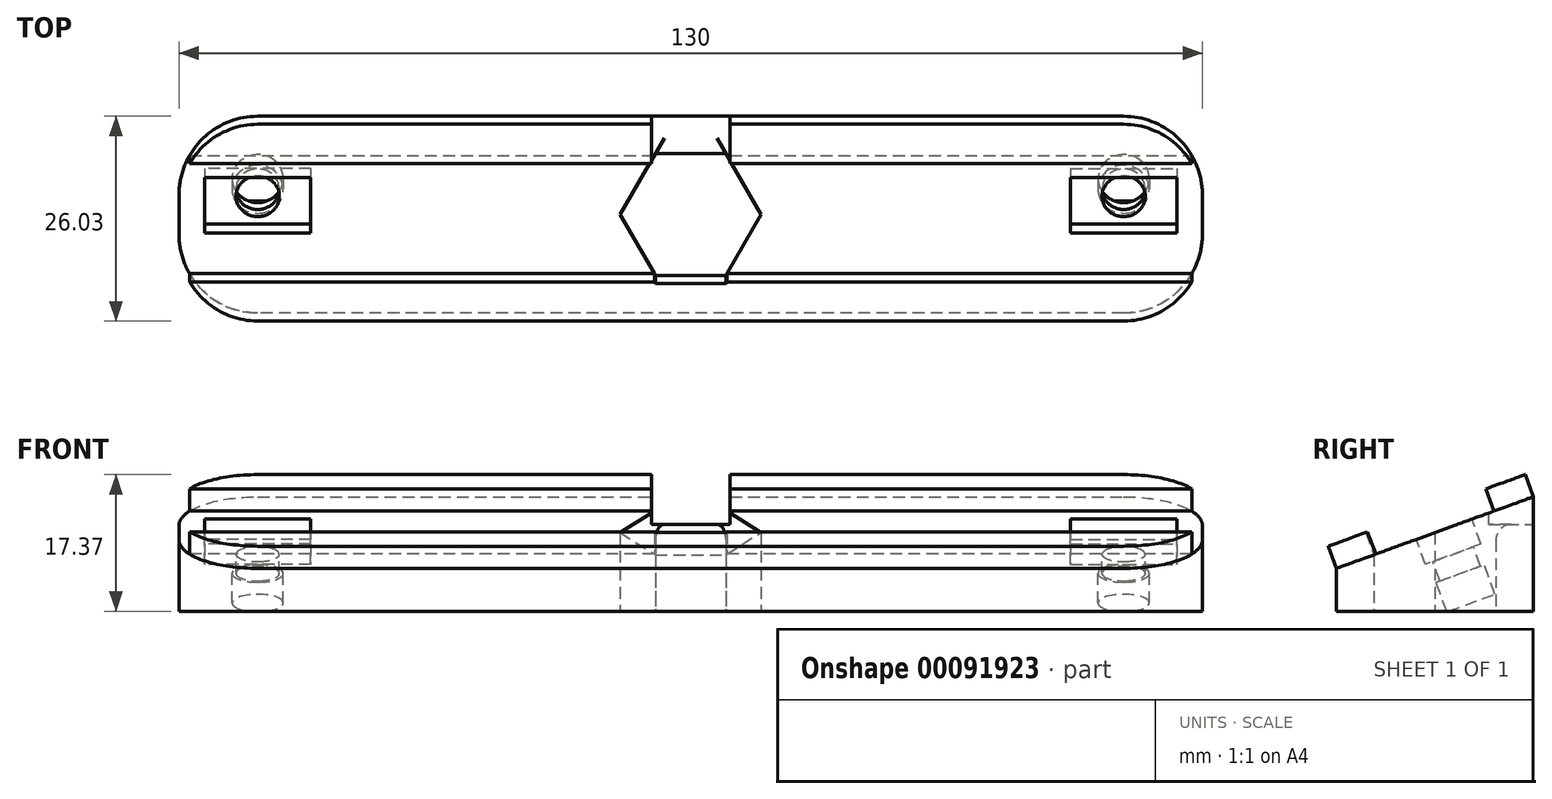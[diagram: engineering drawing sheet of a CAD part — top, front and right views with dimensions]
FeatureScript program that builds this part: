
annotation { "Feature Type Name" : "Feature", "Feature Type Description" : "" }
export const myFeature = defineFeature(function(context is Context, id is Id, definition is map)
    precondition{}
    {
        {
            var Q0;
            Q0=qCreatedBy(makeId("Front.planeOp"),FACE);
            var sketch = newSketch(context, id + "F0", { "sketchPlane" : qUnion([Q0])});
            skLineSegment(sketch, "E0", {"start": v(-41.25, 10) * mm, "end": v(39.47, 10) * mm, "construction": true});
            skSolve(sketch);
        }
        {
            var Q0;
            Q0=sQuery(id+"F0.wireOp",EDGE,"E0");
            cPlane(context, id + "F1", {"entities" : qUnion([Q0]), "cplaneType" : CPlaneType.LINE_ANGLE, "offset" : 150 * mm, "angle" : 290 * degree, "width" : 150 * mm, "height" : 150 * mm});
        }
        {
            var Q0;
            Q0=qCreatedBy(makeId("Top.planeOp"),FACE);
            var sketch = newSketch(context, id + "F2", { "sketchPlane" : qUnion([Q0])});
            skLineSegment(sketch, "E1.bottom", {"start": v(55, 12.5) * mm, "end": v(-55, 12.5) * mm});
            skLineSegment(sketch, "E1.top", {"start": v(55, -12.5) * mm, "end": v(-55, -12.5) * mm});
            skLineSegment(sketch, "E1.left", {"start": v(65, 2.5) * mm, "end": v(65, -2.5) * mm});
            skLineSegment(sketch, "E1.right", {"start": v(-65, 2.5) * mm, "end": v(-65, -2.5) * mm});
            skPoint(sketch, "E1.middle", {"position": v(0, 0) * mm});
            skPoint(sketch, "E2.visualSharp", {"position": v(-65, 12.5) * mm});
            skArc(sketch, "E2.filletArc", {"start": v(-55, 12.5) * mm, "mid": v(-62.07, 9.57) * mm, "end": v(-65, 2.5) * mm});
            skPoint(sketch, "E3.visualSharp", {"position": v(-65, -12.5) * mm});
            skArc(sketch, "E3.filletArc", {"start": v(-65, -2.5) * mm, "mid": v(-62.07, -9.57) * mm, "end": v(-55, -12.5) * mm});
            skPoint(sketch, "E4.visualSharp", {"position": v(65, 12.5) * mm});
            skArc(sketch, "E4.filletArc", {"start": v(65, 2.5) * mm, "mid": v(62.07, 9.57) * mm, "end": v(55, 12.5) * mm});
            skPoint(sketch, "E5.visualSharp", {"position": v(65, -12.5) * mm});
            skArc(sketch, "E5.filletArc", {"start": v(55, -12.5) * mm, "mid": v(62.07, -9.57) * mm, "end": v(65, -2.5) * mm});
            skSolve(sketch);
        }
        {
            var Q0;
            Q0 = qSketchRegion(id + "F2", true);
            var Q1;
            Q1=qCreatedBy(id+"F1.planeOp",FACE);
            extrude(context, id + "F3", {"entities" : qUnion([Q0]), "endBound" : BoundingType.UP_TO_SURFACE, "endBoundEntityFace" : qUnion([Q1]), "depth" : 5.6 * mm});
        }
        {
            var Q0;
            Q0=makeQuery(id+"F3.opExtrude","CAP_FACE",FACE,{"disambiguationData":[OSD([sQuery(id+"F2.wireOp",EDGE,"E1.bottom"),sQuery(id+"F2.wireOp",EDGE,"E1.top"),sQuery(id+"F2.wireOp",EDGE,"E1.left"),sQuery(id+"F2.wireOp",EDGE,"E1.right"),sQuery(id+"F2.wireOp",EDGE,"E2.filletArc"),sQuery(id+"F2.wireOp",EDGE,"E3.filletArc"),sQuery(id+"F2.wireOp",EDGE,"E4.filletArc"),sQuery(id+"F2.wireOp",EDGE,"E5.filletArc")])],"isStart":true});
            var sketch = newSketch(context, id + "F4", { "sketchPlane" : qUnion([Q0])});
            skCircle(sketch, "E6.cCircle", {"center": v(0, 0) * mm, "radius": 7.75 * mm, "construction": true});
            skLineSegment(sketch, "E6.0", {"start": v(4.47, 7.75) * mm, "end": v(8.95, 0) * mm});
            skLineSegment(sketch, "E6.1", {"start": v(8.95, 0) * mm, "end": v(4.47, -7.75) * mm});
            skLineSegment(sketch, "E6.2", {"start": v(4.47, -7.75) * mm, "end": v(-4.47, -7.75) * mm});
            skLineSegment(sketch, "E6.3", {"start": v(-4.47, -7.75) * mm, "end": v(-8.95, 0) * mm});
            skLineSegment(sketch, "E6.4", {"start": v(-8.95, 0) * mm, "end": v(-4.47, 7.75) * mm});
            skLineSegment(sketch, "E6.5", {"start": v(-4.47, 7.75) * mm, "end": v(4.47, 7.75) * mm});
            skPoint(sketch, "E6.0.midPoint", {"position": v(6.71, 3.88) * mm});
            skSolve(sketch);
        }
        {
            var Q0;
            Q0 = qSketchRegion(id + "F4", true);
            extrude(context, id + "F5", {"entities" : qUnion([Q0]), "operationType" : NewBodyOperationType.REMOVE, "endBound" : BoundingType.THROUGH_ALL, "oppositeDirection" : true, "depth" : 7 * mm});
        }
        {
            var Q0;
            Q0=makeQuery(id+"F3.opExtrude","CAP_FACE",FACE,{"disambiguationData":[OSD([sQuery(id+"F2.wireOp",EDGE,"E1.bottom"),sQuery(id+"F2.wireOp",EDGE,"E1.top"),sQuery(id+"F2.wireOp",EDGE,"E1.left"),sQuery(id+"F2.wireOp",EDGE,"E1.right"),sQuery(id+"F2.wireOp",EDGE,"E2.filletArc"),sQuery(id+"F2.wireOp",EDGE,"E3.filletArc"),sQuery(id+"F2.wireOp",EDGE,"E4.filletArc"),sQuery(id+"F2.wireOp",EDGE,"E5.filletArc")])],"isStart":false});
            var sketch = newSketch(context, id + "F6", { "sketchPlane" : qUnion([Q0])});
            skLineSegment(sketch, "E7", {"start": v(-65, 11.42) * mm, "end": v(65, 11.42) * mm});
            skLineSegment(sketch, "E8", {"start": v(65, -4.58) * mm, "end": v(-65, -4.58) * mm});
            skPoint(sketch, "E9", {"position": v(-65, 3.42) * mm});
            skPoint(sketch, "E10", {"position": v(65, 3.42) * mm});
            skLineSegment(sketch, "E11", {"start": v(-65, 3.42) * mm, "end": v(65, 3.42) * mm, "construction": true});
            skSolve(sketch);
        }
        {
            var Q0;
            {var subQ0=sQuery(id+"F6.wireOp",EDGE,"E7");Q0=makeQuery(id+"F6.imprint","IMPRINT",FACE,{"disambiguationData":[TD([[makeQuery(id+"F6.imprint","IMPRINT",EDGE,{"derivedFrom":subQ0}),1.0]])]});}
            var Q1;
            {var subQ0=sQuery(id+"F6.wireOp",EDGE,"E8");Q1=makeQuery(id+"F6.imprint","IMPRINT",FACE,{"disambiguationData":[TD([[makeQuery(id+"F6.imprint","IMPRINT",EDGE,{"derivedFrom":subQ0}),1.0]])]});}
            extrude(context, id + "F7", {"entities" : qUnion([Q0, Q1]), "operationType" : NewBodyOperationType.ADD, "depth" : 3 * mm});
        }
        {
            var Q0;
            {var subQ1=sQuery(id+"F2.wireOp",EDGE,"E5.filletArc");var subQ2=sQuery(id+"F2.wireOp",EDGE,"E4.filletArc");var subQ3=sQuery(id+"F2.wireOp",EDGE,"E3.filletArc");var subQ4=sQuery(id+"F2.wireOp",EDGE,"E2.filletArc");var subQ5=sQuery(id+"F2.wireOp",EDGE,"E1.right");var subQ6=sQuery(id+"F2.wireOp",EDGE,"E1.left");var subQ7=sQuery(id+"F2.wireOp",EDGE,"E1.top");var subQ8=sQuery(id+"F2.wireOp",EDGE,"E1.bottom");var subQ12=makeQuery(id+"F3.opExtrude","CAP_FACE",FACE,{"disambiguationData":[OSD([subQ8,subQ7,subQ6,subQ5,subQ4,subQ3,subQ2,subQ1])],"isStart":false});var subQ15=subQ12;Q0=qUnion([makeQuery(id+"F7.boolean.opBoolean","SPLIT",FACE,{"disambiguationData":[TD([makeQuery(id+"F3.opExtrude","SWEPT_FACE",FACE,{"disambiguationData":[OSD([subQ6])]})])],"derivedFrom":subQ15}),makeQuery(id+"F7.boolean.opBoolean","SPLIT",FACE,{"disambiguationData":[TD([makeQuery(id+"F3.opExtrude","SWEPT_FACE",FACE,{"disambiguationData":[OSD([subQ5])]})])],"derivedFrom":subQ15})]);}
            var sketch = newSketch(context, id + "F8", { "sketchPlane" : qUnion([Q0])});
            skLineSegment(sketch, "E12.bottom", {"start": v(-48.25, 8.42) * mm, "end": v(-61.75, 8.42) * mm});
            skLineSegment(sketch, "E12.top", {"start": v(-48.25, 0.92) * mm, "end": v(-61.75, 0.92) * mm});
            skLineSegment(sketch, "E12.left", {"start": v(-48.25, 8.42) * mm, "end": v(-48.25, 0.92) * mm});
            skLineSegment(sketch, "E12.right", {"start": v(-61.75, 8.42) * mm, "end": v(-61.75, 0.92) * mm});
            skPoint(sketch, "E12.middle", {"position": v(-55, 4.67) * mm});
            skLineSegment(sketch, "E13.MirrorCS", {"start": v(48.25, 0.92) * mm, "end": v(61.75, 0.92) * mm});
            skLineSegment(sketch, "E14.MirrorCS", {"start": v(48.25, 8.42) * mm, "end": v(61.75, 8.42) * mm});
            skLineSegment(sketch, "E15.MirrorCS", {"start": v(61.75, 8.42) * mm, "end": v(61.75, 0.92) * mm});
            skLineSegment(sketch, "E16.MirrorCS", {"start": v(48.25, 8.42) * mm, "end": v(48.25, 0.92) * mm});
            skPoint(sketch, "E17.MirrorP", {"position": v(55, 4.67) * mm});
            skSolve(sketch);
        }
        {
            var Q0;
            Q0 = qSketchRegion(id + "F8", true);
            extrude(context, id + "F9", {"entities" : qUnion([Q0]), "operationType" : NewBodyOperationType.REMOVE, "oppositeDirection" : true, "depth" : 3.38 * mm});
        }
        {
            var Q0;
            Q0=makeQuery(id+"F9.boolean.opBoolean","COPY",FACE,{"derivedFrom":makeQuery(id+"F9.opExtrude","CAP_FACE",FACE,{"disambiguationData":[OSD([sQuery(id+"F8.wireOp",EDGE,"E12.bottom"),sQuery(id+"F8.wireOp",EDGE,"E12.top"),sQuery(id+"F8.wireOp",EDGE,"E12.left"),sQuery(id+"F8.wireOp",EDGE,"E12.right")])],"isStart":false})});
            var sketch = newSketch(context, id + "F10", { "sketchPlane" : qUnion([Q0])});
            skCircle(sketch, "E18", {"center": v(-55, 4.67) * mm, "radius": 2.75 * mm});
            skPoint(sketch, "E18.centerSnap0", {"position": v(-48.25, 4.67) * mm});
            skPoint(sketch, "E18.centerSnap1", {"position": v(-55, 8.42) * mm});
            skCircle(sketch, "E19.MirrorC", {"center": v(55, 4.67) * mm, "radius": 2.75 * mm});
            skSolve(sketch);
        }
        {
            var Q0;
            Q0 = qSketchRegion(id + "F10", true);
            extrude(context, id + "F11", {"entities" : qUnion([Q0]), "operationType" : NewBodyOperationType.REMOVE, "oppositeDirection" : true, "depth" : 2.6 * mm});
        }
        {
            var Q0;
            Q0=makeQuery(id+"F11.boolean.opBoolean","COPY",FACE,{"derivedFrom":makeQuery(id+"F11.opExtrude","CAP_FACE",FACE,{"disambiguationData":[OSD([sQuery(id+"F10.wireOp",EDGE,"E18")])],"isStart":false})});
            var sketch = newSketch(context, id + "F12", { "sketchPlane" : qUnion([Q0])});
            skCircle(sketch, "E20", {"center": v(-55, 4.67) * mm, "radius": 3.25 * mm});
            skCircle(sketch, "E21.MirrorC", {"center": v(55, 4.67) * mm, "radius": 3.25 * mm});
            skSolve(sketch);
        }
        {
            var Q0;
            Q0 = qSketchRegion(id + "F12", true);
            extrude(context, id + "F13", {"entities" : qUnion([Q0]), "operationType" : NewBodyOperationType.REMOVE, "oppositeDirection" : true, "depth" : 4 * mm});
        }
        {
            var Q0;
            Q0=makeQuery(id+"F3.opExtrude","SWEPT_FACE",FACE,{"disambiguationData":[OSD([sQuery(id+"F2.wireOp",EDGE,"E1.bottom")])]});
            var sketch = newSketch(context, id + "F14", { "sketchPlane" : qUnion([Q0])});
            skLineSegment(sketch, "E22.bottom", {"start": v(5, 18.05) * mm, "end": v(-5, 18.05) * mm});
            skLineSegment(sketch, "E22.top", {"start": v(5, 11.05) * mm, "end": v(-5, 11.05) * mm});
            skLineSegment(sketch, "E22.left", {"start": v(5, 18.05) * mm, "end": v(5, 11.05) * mm});
            skLineSegment(sketch, "E22.right", {"start": v(-5, 18.05) * mm, "end": v(-5, 11.05) * mm});
            skPoint(sketch, "E22.middle", {"position": v(0, 14.55) * mm});
            skSolve(sketch);
        }
        {
            var Q0;
            Q0 = qSketchRegion(id + "F14", true);
            extrude(context, id + "F15", {"entities" : qUnion([Q0]), "operationType" : NewBodyOperationType.REMOVE, "endBound" : BoundingType.THROUGH_ALL, "oppositeDirection" : true, "depth" : 25 * mm});
        }
        {
            var Q0;
            Q0=makeQuery(id+"F15.boolean.opBoolean","INTERSECT",EDGE,{"derivedFrom":[makeQuery(id+"F5.boolean.opBoolean","COPY",FACE,{"derivedFrom":makeQuery(id+"F5.opExtrude","SWEPT_FACE",FACE,{"disambiguationData":[OSD([sQuery(id+"F4.wireOp",EDGE,"E6.2")])]})}),makeQuery(id+"F15.opExtrude","SWEPT_FACE",FACE,{"disambiguationData":[OSD([sQuery(id+"F14.wireOp",EDGE,"E22.top")])]})]});
            fillet(context, id + "F16", {"entities" : qUnion([Q0]), "radius" : 2 * mm, "tangentPropagation" : true, "allowEdgeOverflow" : false});
        }
    });
